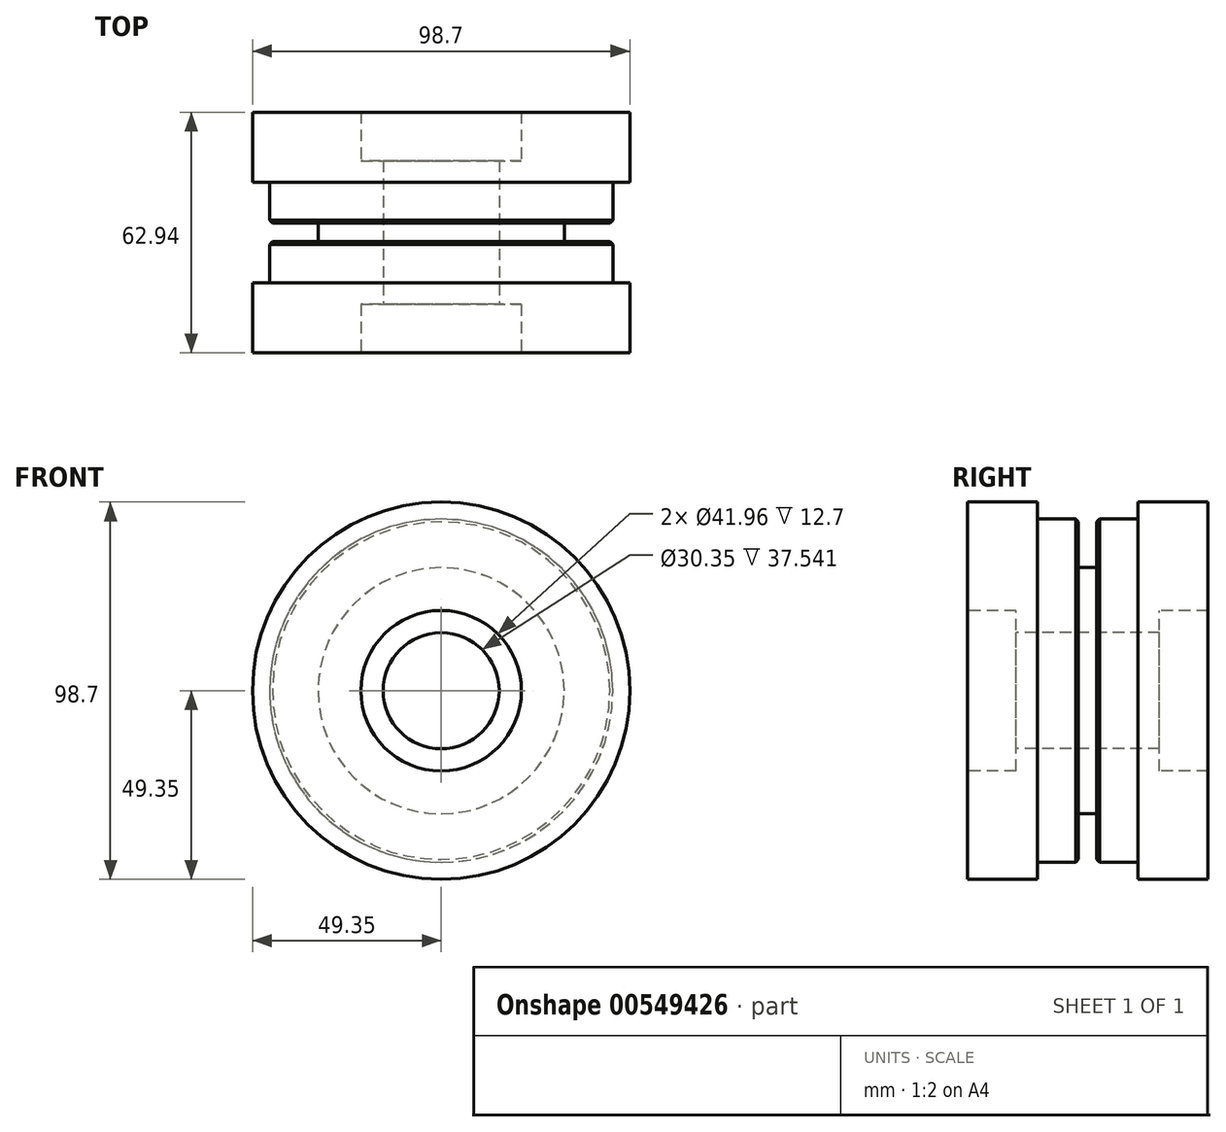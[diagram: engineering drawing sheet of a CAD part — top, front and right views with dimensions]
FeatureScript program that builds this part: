
annotation { "Feature Type Name" : "Feature", "Feature Type Description" : "" }
export const myFeature = defineFeature(function(context is Context, id is Id, definition is map)
    precondition{}
    {
        {
            var Q0;
            Q0=qCreatedBy(makeId("Right.planeOp"),FACE);
            var sketch = newSketch(context, id + "F0", { "sketchPlane" : qUnion([Q0])});
            skLineSegment(sketch, "E0", {"start": v(-35.21, 0) * mm, "end": v(33.24, 0) * mm, "construction": true});
            skLineSegment(sketch, "E1", {"start": v(0, 15.18) * mm, "end": v(-18.77, 15.18) * mm});
            skLineSegment(sketch, "E2", {"start": v(-18.77, 15.18) * mm, "end": v(-18.77, 20.98) * mm});
            skLineSegment(sketch, "E3", {"start": v(-18.77, 20.98) * mm, "end": v(-31.47, 20.98) * mm});
            skLineSegment(sketch, "E4", {"start": v(-31.47, 20.98) * mm, "end": v(-31.47, 49.35) * mm});
            skLineSegment(sketch, "E5", {"start": v(-31.47, 49.35) * mm, "end": v(-13.14, 49.35) * mm});
            skLineSegment(sketch, "E6", {"start": v(-13.14, 49.35) * mm, "end": v(-13.14, 44.88) * mm});
            skLineSegment(sketch, "E7", {"start": v(-13.14, 44.88) * mm, "end": v(-2.4, 44.88) * mm});
            skLineSegment(sketch, "E8", {"start": v(0, 44.88) * mm, "end": v(0, 15.18) * mm, "construction": true});
            skLineSegment(sketch, "E9.MirrorCS", {"start": v(13.14, 44.88) * mm, "end": v(2.4, 44.88) * mm});
            skLineSegment(sketch, "E10.MirrorCS", {"start": v(13.14, 49.35) * mm, "end": v(13.14, 44.88) * mm});
            skLineSegment(sketch, "E11.MirrorCS", {"start": v(31.47, 49.35) * mm, "end": v(13.14, 49.35) * mm});
            skLineSegment(sketch, "E12.MirrorCS", {"start": v(31.47, 20.98) * mm, "end": v(31.47, 49.35) * mm});
            skLineSegment(sketch, "E13.MirrorCS", {"start": v(18.77, 20.98) * mm, "end": v(31.47, 20.98) * mm});
            skLineSegment(sketch, "E14.MirrorCS", {"start": v(18.77, 15.18) * mm, "end": v(18.77, 20.98) * mm});
            skLineSegment(sketch, "E15.MirrorCS", {"start": v(0, 15.18) * mm, "end": v(18.77, 15.18) * mm});
            skLineSegment(sketch, "E16", {"start": v(-2.4, 44.88) * mm, "end": v(-2.4, 32.18) * mm});
            skLineSegment(sketch, "E17", {"start": v(-2.4, 32.18) * mm, "end": v(2.4, 32.18) * mm});
            skLineSegment(sketch, "E18", {"start": v(2.4, 32.18) * mm, "end": v(2.4, 44.88) * mm});
            skPoint(sketch, "E19.orphan", {"position": v(0, 44.88) * mm});
            skSolve(sketch);
        }
        {
            var Q0;
            Q0=qSketchRegion(id+"F0",true);
            var Q1;
            Q1=sQuery(id+"F0.wireOp",EDGE,"E0");
            revolve(context, id + "F1", {"entities" : qUnion([Q0]), "axis" : qUnion([Q1]), "revolveType" : RevolveType.FULL});
        }
        {
            var Q0;
            Q0=makeQuery(id+"F1.opRevolve","SWEPT_EDGE",EDGE,{"disambiguationData":[OSD([sQuery(id+"F0.wireOp",EDGE,"E9.MirrorCS"),sQuery(id+"F0.wireOp",EDGE,"E18")])]});
            var Q1;
            Q1=makeQuery(id+"F1.opRevolve","SWEPT_EDGE",EDGE,{"disambiguationData":[OSD([sQuery(id+"F0.wireOp",EDGE,"E7"),sQuery(id+"F0.wireOp",EDGE,"E16")])]});
            chamfer(context, id + "F2", {"entities" : qUnion([Q0, Q1]), "width" : 0.76 * mm, "tangentPropagation" : true});
        }
        {
            var Q0;
            Q0=makeQuery(id+"F1.opRevolve","SWEPT_EDGE",EDGE,{"disambiguationData":[OSD([sQuery(id+"F0.wireOp",EDGE,"E17"),sQuery(id+"F0.wireOp",EDGE,"E18")])]});
            var Q1;
            Q1=makeQuery(id+"F1.opRevolve","SWEPT_EDGE",EDGE,{"disambiguationData":[OSD([sQuery(id+"F0.wireOp",EDGE,"E16"),sQuery(id+"F0.wireOp",EDGE,"E17")])]});
            fillet(context, id + "F3", {"entities" : qUnion([Q0, Q1]), "radius" : 0.25 * mm, "tangentPropagation" : true, "allowEdgeOverflow" : false});
        }
    });
